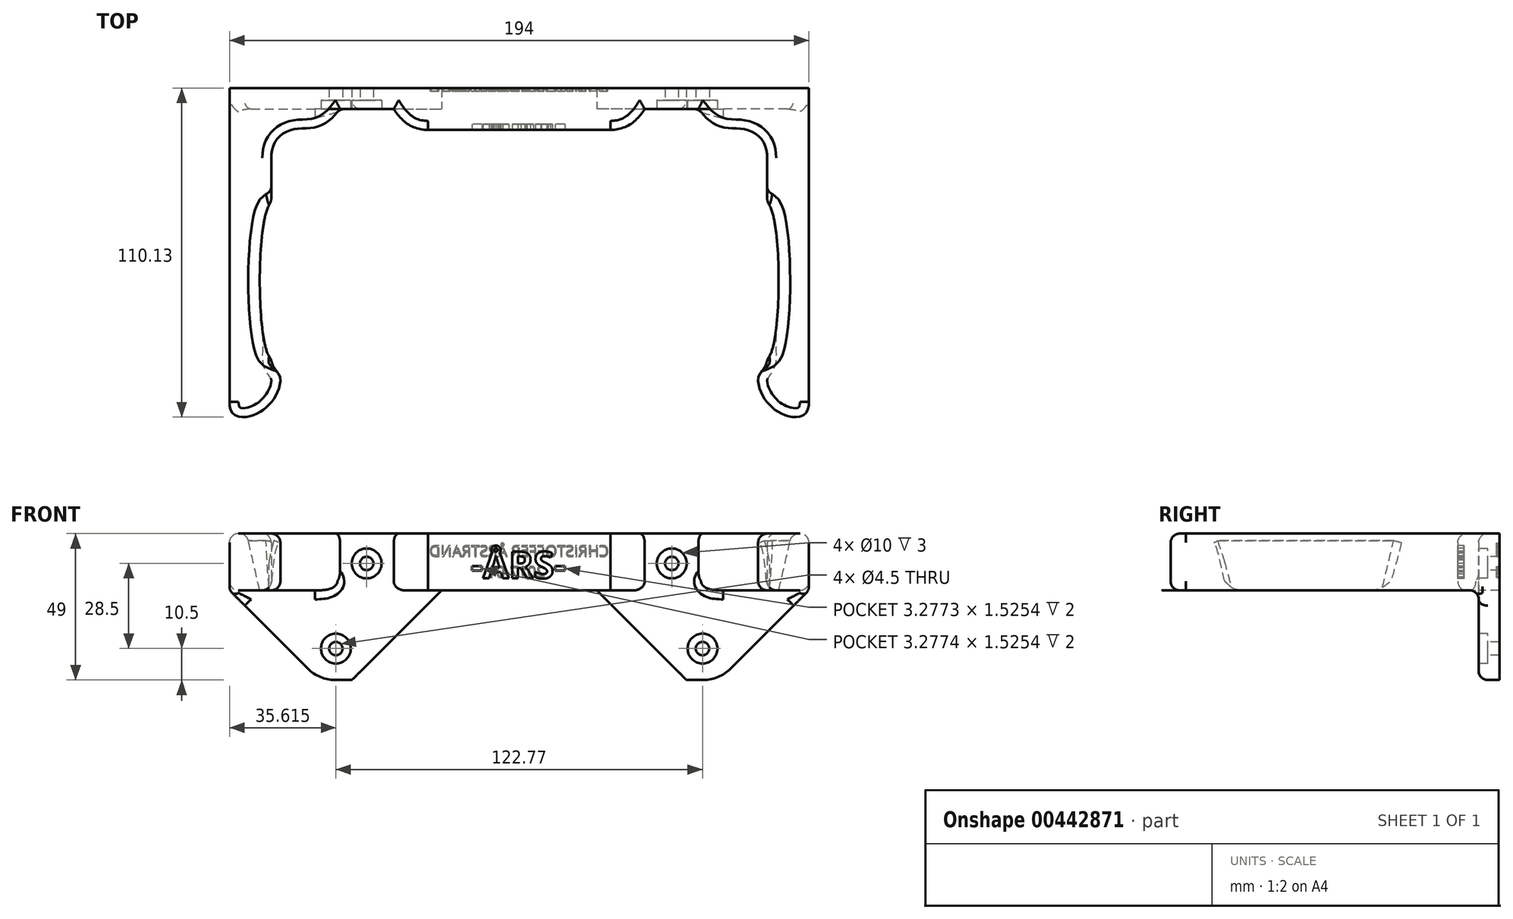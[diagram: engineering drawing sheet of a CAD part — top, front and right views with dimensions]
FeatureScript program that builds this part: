
annotation { "Feature Type Name" : "Feature", "Feature Type Description" : "" }
export const myFeature = defineFeature(function(context is Context, id is Id, definition is map)
    precondition{}
    {
        {
            var Q0;
            Q0=qCreatedBy(makeId("Top.planeOp"),FACE);
            var sketch = newSketch(context, id + "F0", { "sketchPlane" : qUnion([Q0])});
            skLineSegment(sketch, "E0", {"start": v(-97, -55) * mm, "end": v(-97, 50) * mm});
            skLineSegment(sketch, "E1", {"start": v(-83, 35.04) * mm, "end": v(-83, -31.62) * mm});
            skLineSegment(sketch, "E2", {"start": v(-60, -48) * mm, "end": v(-42, -48) * mm});
            skLineSegment(sketch, "E3", {"start": v(-42, -48) * mm, "end": v(-42, -48) * mm});
            skLineSegment(sketch, "E4", {"start": v(-30.59, -41) * mm, "end": v(0, -41) * mm});
            skLineSegment(sketch, "E5", {"start": v(0, -41) * mm, "end": v(0, -55) * mm});
            skLineSegment(sketch, "E6", {"start": v(0, -55) * mm, "end": v(-97, -55) * mm});
            skPoint(sketch, "E7.visualSharp", {"position": v(-42, -41) * mm});
            skFitSpline(sketch, "E8", {"points": [v(-60, -48) * mm, v(-74.68, -41.36) * mm, v(-83, -31.62) * mm], "startDerivative": vector(-34.71, 44.32) * mm, "endDerivative": vector(0, 42.54) * mm});
            skFitSpline(sketch, "E9", {"points": [v(-30.59, -41) * mm, v(-42, -48) * mm], "startDerivative": vector(-9.38, -0.32) * mm, "endDerivative": vector(-11.65, -18.3) * mm});
            skFitSpline(sketch, "E10", {"points": [v(-83, 35.04) * mm, v(-80.16, 41.61) * mm, v(-83.93, 51.2) * mm, v(-93.13, 55.1) * mm, v(-97, 50) * mm], "startDerivative": vector(-0.85, 48.06) * mm, "endDerivative": vector(-0.21, -51.67) * mm});
            skLineSegment(sketch, "E11", {"start": v(-42, -48) * mm, "end": v(-42, -55) * mm});
            skLineSegment(sketch, "E12", {"start": v(-42, -48) * mm, "end": v(0, -48) * mm});
            skLineSegment(sketch, "E13", {"start": v(-60, -48) * mm, "end": v(-60, -55) * mm});
            skLineSegment(sketch, "E14", {"start": v(-60, -48) * mm, "end": v(-97, -48) * mm});
            skSolve(sketch);
        }
        {
            var Q0;
            {var subQ1=sQuery(id+"F0.wireOp",EDGE,"E0");Q0=makeQuery(id+"F0.imprint","IMPRINT",FACE,{"disambiguationData":[TD([[makeQuery(id+"F0.imprint","IMPRINT",EDGE,{"derivedFrom":subQ1}),-1.0]])]});}
            var Q1;
            {var subQ0=sQuery(id+"F0.wireOp",EDGE,"E13");Q1=makeQuery(id+"F0.imprint","IMPRINT",FACE,{"disambiguationData":[TD([[makeQuery(id+"F0.imprint","IMPRINT",EDGE,{"derivedFrom":subQ0}),-1.0]])]});}
            var Q2;
            Q2=makeQuery(id+"F0.imprint","IMPRINT",FACE,{"disambiguationData":[TD([[makeQuery(id+"F0.imprint","IMPRINT",EDGE,{"derivedFrom":sQuery(id+"F0.wireOp",EDGE,"E1")}),-1.0]])]});
            extrude(context, id + "F1", {"entities" : qUnion([Q0, Q1, Q2]), "oppositeDirection" : true, "depth" : 22 * mm, "hasSecondDirection" : true, "secondDirectionOppositeDirection" : true, "secondDirectionDepth" : 3 * mm});
        }
        {
            var Q0;
            Q0=makeQuery(id+"F0.imprint","IMPRINT",FACE,{"disambiguationData":[TD([[makeQuery(id+"F0.imprint","IMPRINT",EDGE,{"derivedFrom":sQuery(id+"F0.wireOp",EDGE,"E2")}),-1.0]])]});
            var Q1;
            {var subQ4=sQuery(id+"F0.wireOp",EDGE,"E11");Q1=makeQuery(id+"F0.imprint","IMPRINT",FACE,{"disambiguationData":[TD([[makeQuery(id+"F0.imprint","IMPRINT",EDGE,{"derivedFrom":subQ4}),1.0]])]});}
            var Q2;
            {var subQ4=sQuery(id+"F0.wireOp",EDGE,"E13");Q2=makeQuery(id+"F0.imprint","IMPRINT",FACE,{"disambiguationData":[TD([[makeQuery(id+"F0.imprint","IMPRINT",EDGE,{"derivedFrom":subQ4}),-1.0]])]});}
            extrude(context, id + "F2", {"entities" : qUnion([Q0, Q1, Q2]), "operationType" : NewBodyOperationType.ADD, "oppositeDirection" : true, "depth" : 22 * mm, "hasSecondDirection" : true, "secondDirectionOppositeDirection" : false, "secondDirectionDepth" : 27 * mm});
        }
        {
            var Q0;
            Q0=makeQuery(id+"F2.opExtrude","CAP_EDGE",EDGE,{"disambiguationData":[OSD([sQuery(id+"F0.wireOp",EDGE,"E0")])],"isStart":true});
            chamfer(context, id + "F3", {"entities" : qUnion([Q0]), "width" : 30 * mm, "tangentPropagation" : true});
        }
        {
            var Q0;
            {var subQ0=sQuery(id+"F0.wireOp",EDGE,"E4");Q0=makeQuery(id+"F0.imprint","IMPRINT",FACE,{"disambiguationData":[TD([[makeQuery(id+"F0.imprint","IMPRINT",EDGE,{"derivedFrom":subQ0}),-1.0]])]});}
            extrude(context, id + "F4", {"entities" : qUnion([Q0]), "operationType" : NewBodyOperationType.ADD, "oppositeDirection" : true, "depth" : 22 * mm, "hasSecondDirection" : true, "secondDirectionOppositeDirection" : true, "secondDirectionDepth" : 3 * mm});
        }
        {
            var Q0;
            Q0=makeQuery(id+"F1.opExtrude","CAP_FACE",FACE,{"disambiguationData":[OSD([sQuery(id+"F0.wireOp",EDGE,"E0"),sQuery(id+"F0.wireOp",EDGE,"E1"),sQuery(id+"F0.wireOp",EDGE,"E6"),sQuery(id+"F0.wireOp",EDGE,"E8"),sQuery(id+"F0.wireOp",EDGE,"E10"),sQuery(id+"F0.wireOp",EDGE,"E13")])],"isStart":true});
            var sketch = newSketch(context, id + "F5", { "sketchPlane" : qUnion([Q0])});
            skLineSegment(sketch, "E15", {"start": v(-83, 35.04) * mm, "end": v(-83, -16.09) * mm});
            skFitSpline(sketch, "E16", {"points": [v(-83, 35.04) * mm, v(-83, -16.09) * mm], "startDerivative": vector(-15.48, -5.6) * mm, "endDerivative": vector(15.48, -6.32) * mm});
            skSolve(sketch);
        }
        {
            var Q0;
            Q0=makeQuery(id+"F5.imprint","IMPRINT",FACE,{"disambiguationData":[TD([[makeQuery(id+"F5.imprint","IMPRINT",EDGE,{"derivedFrom":sQuery(id+"F5.wireOp",EDGE,"E15")}),-1.0]])]});
            extrude(context, id + "F6", {"entities" : qUnion([Q0]), "operationType" : NewBodyOperationType.REMOVE, "oppositeDirection" : true, "depth" : 25 * mm, "hasDraft" : true, "draftAngle" : 13 * degree});
        }
        {
            var Q0;
            Q0=makeQuery(id+"F2.opExtrude","SWEPT_FACE",FACE,{"disambiguationData":[OSD([sQuery(id+"F0.wireOp",EDGE,"E2"),sQuery(id+"F0.wireOp",EDGE,"E12"),sQuery(id+"F0.wireOp",EDGE,"E14")])]});
            var sketch = newSketch(context, id + "F7", { "sketchPlane" : qUnion([Q0])});
            skLineSegment(sketch, "E17", {"start": v(56, 27) * mm, "end": v(26, -3) * mm});
            skSolve(sketch);
        }
        {
            var Q0;
            {var subQ0=sQuery(id+"F7.wireOp",EDGE,"E17");Q0=makeQuery(id+"F7.imprint","IMPRINT",FACE,{"disambiguationData":[TD([[makeQuery(id+"F7.imprint","IMPRINT",EDGE,{"derivedFrom":subQ0}),-1.0]])]});}
            extrude(context, id + "F8", {"entities" : qUnion([Q0]), "operationType" : NewBodyOperationType.REMOVE, "oppositeDirection" : true, "depth" : 25 * mm});
        }
        {
            var Q0;
            {var subQ0=sQuery(id+"F0.wireOp",EDGE,"E0");Q0=makeQuery(id+"F3.opChamfer","BLEND_EDGE",EDGE,{"blendedFrom":[makeQuery(id+"F2.opExtrude","CAP_EDGE",EDGE,{"disambiguationData":[OSD([subQ0])],"isStart":true}),makeQuery(id+"F2.opExtrude","CAP_FACE",FACE,{"disambiguationData":[OSD([subQ0,sQuery(id+"F0.wireOp",EDGE,"E2"),sQuery(id+"F0.wireOp",EDGE,"E5"),sQuery(id+"F0.wireOp",EDGE,"E6"),sQuery(id+"F0.wireOp",EDGE,"E12"),sQuery(id+"F0.wireOp",EDGE,"E14")])],"isStart":true})],"blendedInto":[makeQuery(id+"F2.opExtrude","CAP_FACE",FACE,{"disambiguationData":[OSD([subQ0,sQuery(id+"F0.wireOp",EDGE,"E2"),sQuery(id+"F0.wireOp",EDGE,"E5"),sQuery(id+"F0.wireOp",EDGE,"E6"),sQuery(id+"F0.wireOp",EDGE,"E12"),sQuery(id+"F0.wireOp",EDGE,"E14")])],"isStart":true})]});}
            var Q1;
            Q1=makeQuery(id+"F8.boolean.opBoolean","COPY",EDGE,{"derivedFrom":makeQuery(id+"F8.opExtrude","SWEPT_EDGE",EDGE,{"disambiguationData":[OSD([sQuery(id+"F0.wireOp",EDGE,"E2"),sQuery(id+"F0.wireOp",EDGE,"E12"),sQuery(id+"F0.wireOp",EDGE,"E14"),sQuery(id+"F7.wireOp",EDGE,"E17")])]})});
            fillet(context, id + "F9", {"entities" : qUnion([Q0, Q1]), "radius" : 13 * mm, "tangentPropagation" : true, "allowEdgeOverflow" : false});
        }
        {
            var Q0;
            Q0=makeQuery(id+"F1.opExtrude","CAP_EDGE",EDGE,{"disambiguationData":[OSD([sQuery(id+"F0.wireOp",EDGE,"E8")])],"isStart":false});
            var Q1;
            Q1=makeQuery(id+"F1.opExtrude","CAP_EDGE",EDGE,{"disambiguationData":[OSD([sQuery(id+"F0.wireOp",EDGE,"E8")])],"isStart":true});
            var Q2;
            Q2=makeQuery(id+"F1.opExtrude","CAP_EDGE",EDGE,{"disambiguationData":[OSD([sQuery(id+"F0.wireOp",EDGE,"E1")])],"isStart":false});
            var Q3;
            Q3=makeQuery(id+"F1.opExtrude","CAP_EDGE",EDGE,{"disambiguationData":[OSD([sQuery(id+"F0.wireOp",EDGE,"E1")])],"isStart":true});
            var Q4;
            Q4=makeQuery(id+"F1.opExtrude","CAP_EDGE",EDGE,{"disambiguationData":[OSD([sQuery(id+"F0.wireOp",EDGE,"E10")])],"isStart":true});
            var Q5;
            Q5=makeQuery(id+"F1.opExtrude","CAP_EDGE",EDGE,{"disambiguationData":[OSD([sQuery(id+"F0.wireOp",EDGE,"E10")])],"isStart":false});
            var Q6;
            Q6=makeQuery(id+"F1.opExtrude","CAP_EDGE",EDGE,{"disambiguationData":[OSD([sQuery(id+"F0.wireOp",EDGE,"E0")])],"isStart":false});
            var Q7;
            Q7=makeQuery(id+"F1.opExtrude","CAP_EDGE",EDGE,{"disambiguationData":[OSD([sQuery(id+"F0.wireOp",EDGE,"E0")])],"isStart":true});
            var Q8;
            Q8=makeQuery(id+"F2.opExtrude","CAP_EDGE",EDGE,{"disambiguationData":[OSD([sQuery(id+"F0.wireOp",EDGE,"E2"),sQuery(id+"F0.wireOp",EDGE,"E12")])],"isStart":false});
            var Q9;
            Q9=makeQuery(id+"F4.opExtrude","CAP_EDGE",EDGE,{"disambiguationData":[OSD([sQuery(id+"F0.wireOp",EDGE,"E9")])],"isStart":false});
            var Q10;
            Q10=makeQuery(id+"F4.opExtrude","CAP_EDGE",EDGE,{"disambiguationData":[OSD([sQuery(id+"F0.wireOp",EDGE,"E4")])],"isStart":false});
            var Q11;
            Q11=makeQuery(id+"F4.opExtrude","CAP_EDGE",EDGE,{"disambiguationData":[OSD([sQuery(id+"F0.wireOp",EDGE,"E9")])],"isStart":true});
            var Q12;
            Q12=makeQuery(id+"F4.opExtrude","CAP_EDGE",EDGE,{"disambiguationData":[OSD([sQuery(id+"F0.wireOp",EDGE,"E4")])],"isStart":true});
            var Q13;
            {var subQ0=sQuery(id+"F0.wireOp",EDGE,"E12");var subQ1=sQuery(id+"F0.wireOp",EDGE,"E5");var subQ2=sQuery(id+"F0.wireOp",EDGE,"E13");var subQ3=sQuery(id+"F0.wireOp",EDGE,"E6");Q13=makeQuery(id+"F6.boolean.opBoolean","INTERSECT",EDGE,{"derivedFrom":[makeQuery(id+"F4.boolean.opBoolean","MERGE",FACE,{"derivedFrom":[makeQuery(id+"F2.boolean.opBoolean","MERGE",FACE,{"derivedFrom":[makeQuery(id+"F1.opExtrude","CAP_FACE",FACE,{"disambiguationData":[OSD([sQuery(id+"F0.wireOp",EDGE,"E0"),sQuery(id+"F0.wireOp",EDGE,"E1"),subQ3,sQuery(id+"F0.wireOp",EDGE,"E8"),sQuery(id+"F0.wireOp",EDGE,"E10"),subQ2])],"isStart":false}),makeQuery(id+"F2.opExtrude","CAP_FACE",FACE,{"disambiguationData":[OSD([sQuery(id+"F0.wireOp",EDGE,"E2"),subQ1,subQ3,subQ0,subQ2])],"isStart":false})]}),makeQuery(id+"F4.opExtrude","CAP_FACE",FACE,{"disambiguationData":[OSD([sQuery(id+"F0.wireOp",EDGE,"E4"),subQ1,sQuery(id+"F0.wireOp",EDGE,"E9"),subQ0])],"isStart":false})]}),makeQuery(id+"F6.opExtrude","SWEPT_FACE",FACE,{"disambiguationData":[OSD([sQuery(id+"F5.wireOp",EDGE,"E16")])]})]});}
            var Q14;
            Q14=makeQuery(id+"F6.boolean.opBoolean","COPY",EDGE,{"derivedFrom":makeQuery(id+"F6.opExtrude","CAP_EDGE",EDGE,{"disambiguationData":[OSD([sQuery(id+"F5.wireOp",EDGE,"E16")])],"isStart":true})});
            var Q15;
            Q15=makeQuery(id+"F6.boolean.opBoolean","INTERSECT",EDGE,{"derivedFrom":[makeQuery(id+"F1.opExtrude","SWEPT_FACE",FACE,{"disambiguationData":[OSD([sQuery(id+"F0.wireOp",EDGE,"E1")])]}),makeQuery(id+"F6.opExtrude","SWEPT_FACE",FACE,{"disambiguationData":[OSD([sQuery(id+"F5.wireOp",EDGE,"E16")])]})]});
            var Q16;
            Q16=makeQuery(id+"F6.boolean.opBoolean","INTERSECT",EDGE,{"derivedFrom":[makeQuery(id+"F1.opExtrude","SWEPT_FACE",FACE,{"disambiguationData":[OSD([sQuery(id+"F0.wireOp",EDGE,"E10")])]}),makeQuery(id+"F6.opExtrude","SWEPT_FACE",FACE,{"disambiguationData":[OSD([sQuery(id+"F5.wireOp",EDGE,"E16")])]})]});
            var Q17;
            Q17=makeQuery(id+"F2.boolean.opBoolean","INTERSECT",EDGE,{"derivedFrom":[makeQuery(id+"F1.opExtrude","CAP_FACE",FACE,{"disambiguationData":[OSD([sQuery(id+"F0.wireOp",EDGE,"E0"),sQuery(id+"F0.wireOp",EDGE,"E1"),sQuery(id+"F0.wireOp",EDGE,"E6"),sQuery(id+"F0.wireOp",EDGE,"E8"),sQuery(id+"F0.wireOp",EDGE,"E10"),sQuery(id+"F0.wireOp",EDGE,"E13")])],"isStart":true}),makeQuery(id+"F2.opExtrude","SWEPT_FACE",FACE,{"disambiguationData":[OSD([sQuery(id+"F0.wireOp",EDGE,"E2"),sQuery(id+"F0.wireOp",EDGE,"E12"),sQuery(id+"F0.wireOp",EDGE,"E14")])]})]});
            var Q18;
            Q18=makeQuery(id+"F4.opExtrude","CAP_EDGE",EDGE,{"disambiguationData":[OSD([sQuery(id+"F0.wireOp",EDGE,"E12")])],"isStart":true});
            var Q19;
            Q19=makeQuery(id+"F3.opChamfer","BLEND_EDGE",EDGE,{"blendedFrom":[makeQuery(id+"F2.opExtrude","CAP_EDGE",EDGE,{"disambiguationData":[OSD([sQuery(id+"F0.wireOp",EDGE,"E0")])],"isStart":true}),makeQuery(id+"F2.opExtrude","SWEPT_FACE",FACE,{"disambiguationData":[OSD([sQuery(id+"F0.wireOp",EDGE,"E2"),sQuery(id+"F0.wireOp",EDGE,"E12"),sQuery(id+"F0.wireOp",EDGE,"E14")])]})],"blendedInto":[makeQuery(id+"F2.opExtrude","SWEPT_FACE",FACE,{"disambiguationData":[OSD([sQuery(id+"F0.wireOp",EDGE,"E2"),sQuery(id+"F0.wireOp",EDGE,"E12"),sQuery(id+"F0.wireOp",EDGE,"E14")])]})]});
            var Q20;
            {var subQ0=sQuery(id+"F0.wireOp",EDGE,"E14");var subQ1=sQuery(id+"F0.wireOp",EDGE,"E12");var subQ2=sQuery(id+"F0.wireOp",EDGE,"E2");var subQ3=sQuery(id+"F0.wireOp",EDGE,"E0");Q20=makeQuery(id+"F9.opFillet","BLEND_EDGE",EDGE,{"blendedFrom":[makeQuery(id+"F3.opChamfer","BLEND_EDGE",EDGE,{"blendedFrom":[makeQuery(id+"F2.opExtrude","CAP_EDGE",EDGE,{"disambiguationData":[OSD([subQ3])],"isStart":true}),makeQuery(id+"F2.opExtrude","CAP_FACE",FACE,{"disambiguationData":[OSD([subQ3,subQ2,sQuery(id+"F0.wireOp",EDGE,"E5"),sQuery(id+"F0.wireOp",EDGE,"E6"),subQ1,subQ0])],"isStart":true})],"blendedInto":[makeQuery(id+"F2.opExtrude","CAP_FACE",FACE,{"disambiguationData":[OSD([subQ3,subQ2,sQuery(id+"F0.wireOp",EDGE,"E5"),sQuery(id+"F0.wireOp",EDGE,"E6"),subQ1,subQ0])],"isStart":true})]}),makeQuery(id+"F2.opExtrude","SWEPT_FACE",FACE,{"disambiguationData":[OSD([subQ2,subQ1,subQ0])]})],"blendedInto":[makeQuery(id+"F2.opExtrude","SWEPT_FACE",FACE,{"disambiguationData":[OSD([subQ2,subQ1,subQ0])]})]});}
            var Q21;
            Q21=makeQuery(id+"F2.opExtrude","CAP_EDGE",EDGE,{"disambiguationData":[OSD([sQuery(id+"F0.wireOp",EDGE,"E2"),sQuery(id+"F0.wireOp",EDGE,"E12"),sQuery(id+"F0.wireOp",EDGE,"E14")])],"isStart":true});
            var Q22;
            {var subQ0=sQuery(id+"F0.wireOp",EDGE,"E0");Q22=makeQuery(id+"F3.opChamfer","BLEND_EDGE",EDGE,{"blendedFrom":[makeQuery(id+"F2.opExtrude","CAP_EDGE",EDGE,{"disambiguationData":[OSD([subQ0])],"isStart":true}),makeQuery(id+"F2.boolean.opBoolean","MERGE",FACE,{"derivedFrom":[makeQuery(id+"F1.opExtrude","SWEPT_FACE",FACE,{"disambiguationData":[OSD([subQ0])]}),makeQuery(id+"F2.opExtrude","SWEPT_FACE",FACE,{"disambiguationData":[OSD([subQ0])]})]})],"blendedInto":[makeQuery(id+"F2.boolean.opBoolean","MERGE",FACE,{"derivedFrom":[makeQuery(id+"F1.opExtrude","SWEPT_FACE",FACE,{"disambiguationData":[OSD([subQ0])]}),makeQuery(id+"F2.opExtrude","SWEPT_FACE",FACE,{"disambiguationData":[OSD([subQ0])]})]})]});}
            fillet(context, id + "F10", {"entities" : qUnion([Q0, Q1, Q2, Q3, Q4, Q5, Q6, Q7, Q8, Q9, Q10, Q11, Q12, Q13, Q14, Q15, Q16, Q17, Q18, Q19, Q20, Q21, Q22]), "radius" : 3 * mm, "tangentPropagation" : true, "allowEdgeOverflow" : false});
        }
        {
            var Q0;
            Q0=makeQuery(id+"F2.opExtrude","SWEPT_FACE",FACE,{"disambiguationData":[OSD([sQuery(id+"F0.wireOp",EDGE,"E2"),sQuery(id+"F0.wireOp",EDGE,"E12")])]});
            var sketch = newSketch(context, id + "F11", { "sketchPlane" : qUnion([Q0])});
            skCircle(sketch, "E18", {"center": v(51.08, -12) * mm, "radius": 5 * mm});
            skPoint(sketch, "E18.centerSnap0", {"position": v(51.08, -19) * mm});
            skPoint(sketch, "E18.centerSnap1", {"position": v(46.08, -12) * mm});
            skCircle(sketch, "E19", {"center": v(51.08, -12) * mm, "radius": 2.25 * mm});
            skCircle(sketch, "E20", {"center": v(61.38, 16.5) * mm, "radius": 5 * mm});
            skCircle(sketch, "E21", {"center": v(61.38, 16.5) * mm, "radius": 2.25 * mm});
            skSolve(sketch);
        }
        {
            var Q0;
            Q0 = qSketchRegion(id + "F11", true);
            var Q1;
            Q1=sQuery(id+"F11.wireOp",EDGE,"E19");
            extrude(context, id + "F12", {"entities" : qUnion([Q0]), "operationType" : NewBodyOperationType.REMOVE, "surfaceEntities" : qUnion([Q1]), "oppositeDirection" : true, "depth" : 3 * mm});
        }
        {
            var Q0;
            Q0=makeQuery(id+"F11.imprint","IMPRINT",FACE,{"disambiguationData":[TD([[makeQuery(id+"F11.imprint","IMPRINT",EDGE,{"derivedFrom":sQuery(id+"F11.wireOp",EDGE,"E21")}),1.0]])]});
            var Q1;
            Q1=makeQuery(id+"F11.imprint","IMPRINT",FACE,{"disambiguationData":[TD([[makeQuery(id+"F11.imprint","IMPRINT",EDGE,{"derivedFrom":sQuery(id+"F11.wireOp",EDGE,"E19")}),1.0]])]});
            var Q2;
            Q2=sQuery(id+"F11.wireOp",EDGE,"E19");
            extrude(context, id + "F13", {"entities" : qUnion([Q0, Q1]), "operationType" : NewBodyOperationType.REMOVE, "surfaceEntities" : qUnion([Q2]), "oppositeDirection" : true, "depth" : 25 * mm});
        }
        {
            var Q0;
            Q0=makeQuery(id+"F1.opExtrude","SWEPT_BODY",BODY,{"disambiguationData":[OSD([sQuery(id+"F0.wireOp",EDGE,"E0"),sQuery(id+"F0.wireOp",EDGE,"E1"),sQuery(id+"F0.wireOp",EDGE,"E6"),sQuery(id+"F0.wireOp",EDGE,"E8"),sQuery(id+"F0.wireOp",EDGE,"E10"),sQuery(id+"F0.wireOp",EDGE,"E13")])]});
            var Q1;
            Q1=qCreatedBy(makeId("Right.planeOp"),FACE);
            mirror(context, id + "F14", {"operationType" : NewBodyOperationType.ADD, "entities" : qUnion([Q0]), "mirrorPlane" : qUnion([Q1])});
        }
        {
            var Q0;
            Q0=qCreatedBy(makeId("Front.planeOp"),FACE);
            var sketch = newSketch(context, id + "F15", { "sketchPlane" : qUnion([Q0])});
            skLineSegment(sketch, "E22", {"start": v(0, 27) * mm, "end": v(0, -22) * mm});
            skLineSegment(sketch, "E23", {"start": v(-30, 0) * mm, "end": v(30, 0) * mm});
            skSolve(sketch);
        }
        {
            var Q0;
            Q0=makeQuery(id+"F1.opExtrude","SWEPT_BODY",BODY,{"disambiguationData":[OSD([sQuery(id+"F0.wireOp",EDGE,"E0"),sQuery(id+"F0.wireOp",EDGE,"E1"),sQuery(id+"F0.wireOp",EDGE,"E6"),sQuery(id+"F0.wireOp",EDGE,"E8"),sQuery(id+"F0.wireOp",EDGE,"E10"),sQuery(id+"F0.wireOp",EDGE,"E13")])]});
            var Q1;
            Q1=sQuery(id+"F15.wireOp",EDGE,"E23");
            transform(context, id + "F16", {"entities" : qUnion([Q0]), "transformType" : TransformType.ROTATION, "transformAxis" : qUnion([Q1]), "angle" : 180 * degree, "makeCopy" : false});
        }
        {
            var Q0;
            {var subQ0=makeQuery(id+"F4.opExtrude","SWEPT_FACE",FACE,{"disambiguationData":[OSD([sQuery(id+"F0.wireOp",EDGE,"E4")])]});Q0=makeQuery(id+"F14.boolean.opBoolean","MERGE",FACE,{"derivedFrom":[subQ0,makeQuery(id+"F14.opPattern","COPY",FACE,{"derivedFrom":subQ0,"instanceName":"1"})]});}
            var sketch = newSketch(context, id + "F17", { "sketchPlane" : qUnion([Q0])});
            skText(sketch, "E24", { "text": "-ÅRS-", "fontName": "OpenSans-Bold.ttf"});
            const initialGuessF17  = {"E24": [-0.01612, 0.007, 1, 0, 0.009]};
            skSetInitialGuess(sketch, initialGuessF17);
            skSolve(sketch);
        }
        {
            var Q0;
            Q0 = qSketchRegion(id + "F17", true);
            extrude(context, id + "F18", {"entities" : qUnion([Q0]), "operationType" : NewBodyOperationType.REMOVE, "oppositeDirection" : true, "depth" : 2 * mm});
        }
        {
            var Q0;
            {var subQ0=sQuery(id+"F0.wireOp",EDGE,"E6");var subQ1=makeQuery(id+"F2.boolean.opBoolean","MERGE",FACE,{"derivedFrom":[makeQuery(id+"F1.opExtrude","SWEPT_FACE",FACE,{"disambiguationData":[OSD([subQ0])]}),makeQuery(id+"F2.opExtrude","SWEPT_FACE",FACE,{"disambiguationData":[OSD([subQ0])]})]});Q0=makeQuery(id+"F14.boolean.opBoolean","MERGE",FACE,{"derivedFrom":[subQ1,makeQuery(id+"F14.opPattern","COPY",FACE,{"derivedFrom":subQ1,"instanceName":"1"})]});}
            var sketch = newSketch(context, id + "F19", { "sketchPlane" : qUnion([Q0])});
            skText(sketch, "E25", { "text": "CHRISTOFFER ÅRSTRAND\n                2017-01", "fontName": "OpenSans-Regular.ttf"});
            const initialGuessF19  = {"E25": [-0.03, 0.0143, 1, 0, 0.0037]};
            skSetInitialGuess(sketch, initialGuessF19);
            skSolve(sketch);
        }
        {
            var Q0;
            Q0 = qSketchRegion(id + "F19", true);
            extrude(context, id + "F20", {"entities" : qUnion([Q0]), "operationType" : NewBodyOperationType.REMOVE, "oppositeDirection" : true, "depth" : 1 * mm});
        }
    });
